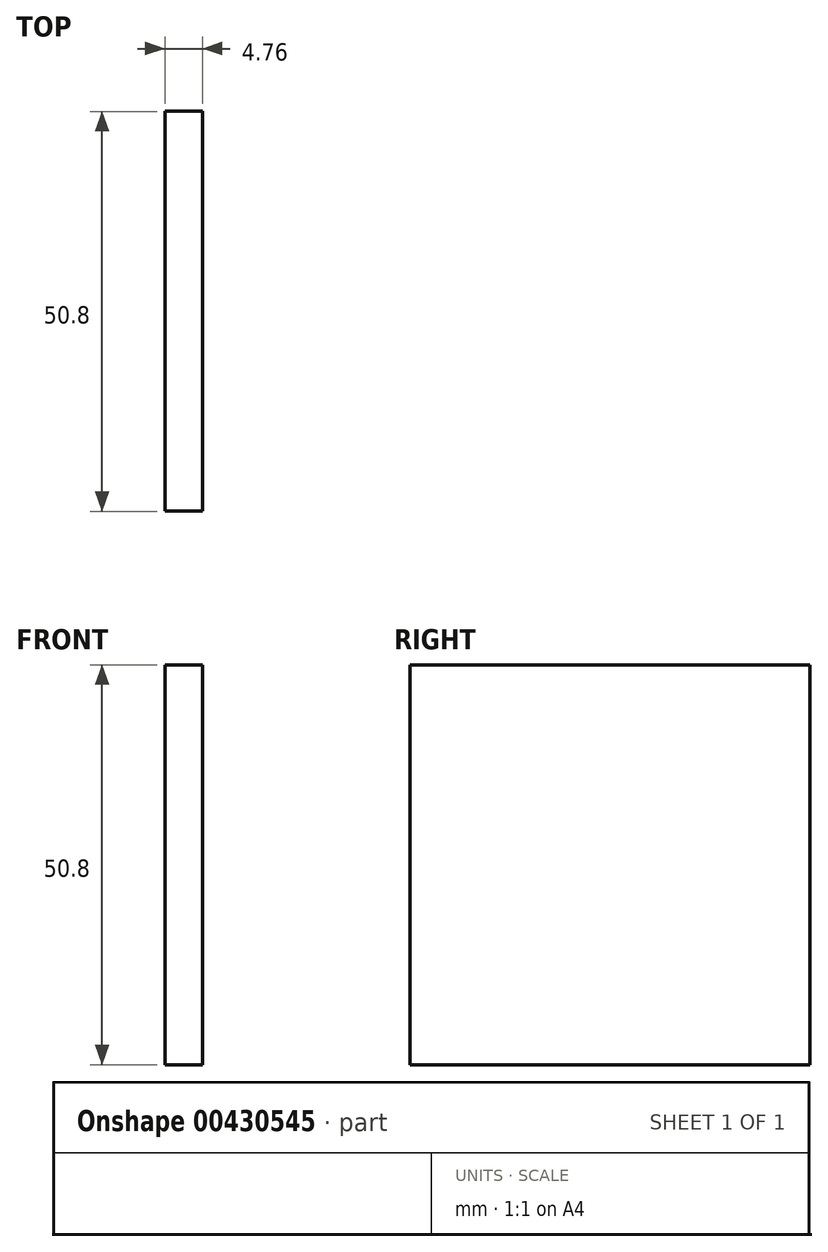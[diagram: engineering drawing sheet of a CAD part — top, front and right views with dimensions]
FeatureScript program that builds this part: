
annotation { "Feature Type Name" : "Feature", "Feature Type Description" : "" }
export const myFeature = defineFeature(function(context is Context, id is Id, definition is map)
    precondition{}
    {
        {
            var Q0;
            Q0=qCreatedBy(makeId("Right.planeOp"),FACE);
            var sketch = newSketch(context, id + "F0", { "sketchPlane" : qUnion([Q0])});
            skLineSegment(sketch, "E0.bottom", {"start": v(-50.29, 4.5) * mm, "end": v(0.51, 4.5) * mm});
            skLineSegment(sketch, "E0.top", {"start": v(-50.29, -46.3) * mm, "end": v(0.51, -46.3) * mm});
            skLineSegment(sketch, "E0.left", {"start": v(-50.29, 4.5) * mm, "end": v(-50.29, -46.3) * mm});
            skLineSegment(sketch, "E0.right", {"start": v(0.51, 4.5) * mm, "end": v(0.51, -46.3) * mm});
            skSolve(sketch);
        }
        {
            var Q0;
            Q0=makeQuery(id+"F0.imprint","IMPRINT",FACE,{"disambiguationData":[TD([[makeQuery(id+"F0.imprint","IMPRINT",EDGE,{"derivedFrom":sQuery(id+"F0.wireOp",EDGE,"E0.bottom")}),-1.0]])]});
            extrude(context, id + "F1", {"entities" : qUnion([Q0]), "depth" : 4.76 * mm});
        }
    });
